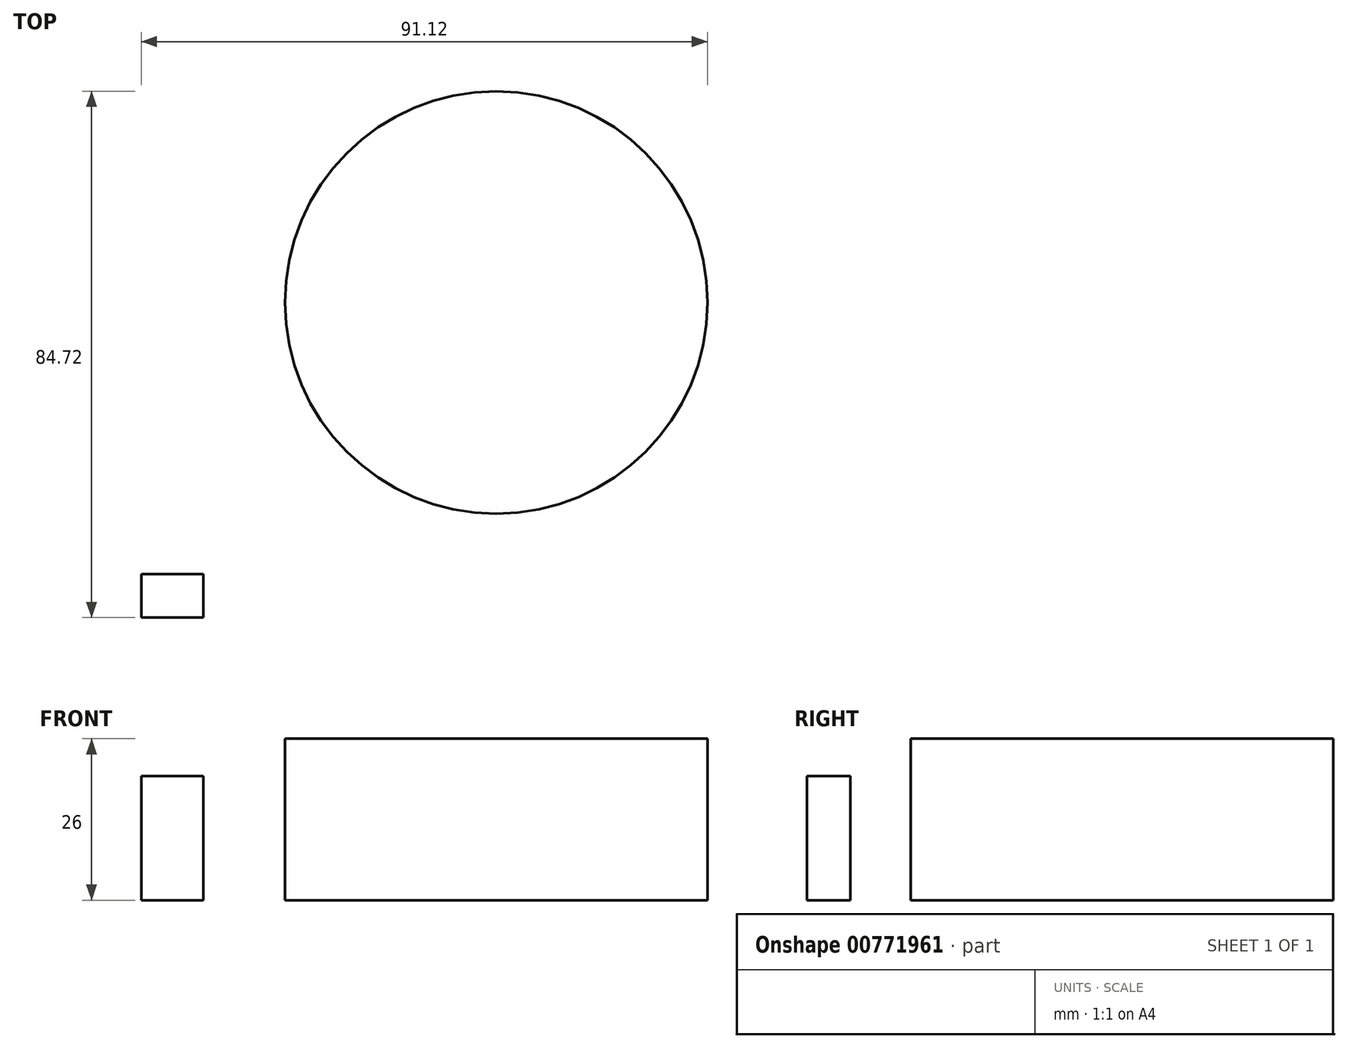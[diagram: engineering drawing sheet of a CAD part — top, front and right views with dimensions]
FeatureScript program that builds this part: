
annotation { "Feature Type Name" : "Feature", "Feature Type Description" : "" }
export const myFeature = defineFeature(function(context is Context, id is Id, definition is map)
    precondition{}
    {
        {
            var Q0;
            Q0=qCreatedBy(makeId("Top.planeOp"),FACE);
            var sketch = newSketch(context, id + "F0", { "sketchPlane" : qUnion([Q0])});
            skCircle(sketch, "E0", {"center": v(0, 0) * mm, "radius": 34 * mm});
            skCircle(sketch, "E1", {"center": v(0, 0) * mm, "radius": 1.5 * mm});
            skLineSegment(sketch, "E2", {"start": v(0, 1.5) * mm, "end": v(0, -1.5) * mm});
            skLineSegment(sketch, "E3", {"start": v(0, 1.5) * mm, "end": v(0, -1) * mm});
            skLineSegment(sketch, "E4", {"start": v(-1.12, -1) * mm, "end": v(1.12, -1) * mm});
            skSolve(sketch);
        }
        {
            var Q0;
            Q0 = qSketchRegion(id + "F0", true);
            var Q1;
            {var subQ0=sQuery(id+"F0.wireOp",EDGE,"E2");Q1=makeQuery(id+"F0.imprint","IMPRINT",FACE,{"disambiguationData":[TD([[makeQuery(id+"F0.imprint","IMPRINT",EDGE,{"derivedFrom":subQ0}),-1.0]])]});}
            var Q2;
            {var subQ0=sQuery(id+"F0.wireOp",EDGE,"E2");Q2=makeQuery(id+"F0.imprint","IMPRINT",FACE,{"disambiguationData":[TD([[makeQuery(id+"F0.imprint","IMPRINT",EDGE,{"derivedFrom":subQ0}),1.0]])]});}
            extrude(context, id + "F1", {"entities" : qUnion([Q0, Q1, Q2]), "depth" : 26 * mm, "offsetDistance" : 25 * mm});
        }
        {
            var Q0;
            Q0=qCreatedBy(makeId("Top.planeOp"),FACE);
            var sketch = newSketch(context, id + "F2", { "sketchPlane" : qUnion([Q0])});
            skCircle(sketch, "E5", {"center": v(-52.12, -47.22) * mm, "radius": 6.1 * mm});
            skLineSegment(sketch, "E6", {"start": v(-57.12, -43.72) * mm, "end": v(-57.12, -50.72) * mm});
            skLineSegment(sketch, "E7", {"start": v(-57.12, -50.72) * mm, "end": v(-47.12, -50.72) * mm});
            skLineSegment(sketch, "E8", {"start": v(-47.12, -50.72) * mm, "end": v(-47.12, -43.72) * mm});
            skLineSegment(sketch, "E9", {"start": v(-47.12, -43.72) * mm, "end": v(-57.12, -43.72) * mm});
            skSolve(sketch);
        }
        {
            var Q0;
            Q0=makeQuery(id+"F2.imprint","IMPRINT",FACE,{"disambiguationData":[TD([[makeQuery(id+"F2.imprint","IMPRINT",EDGE,{"derivedFrom":sQuery(id+"F2.wireOp",EDGE,"E6")}),1.0]])]});
            extrude(context, id + "F3", {"entities" : qUnion([Q0]), "depth" : 20 * mm, "offsetDistance" : 25 * mm});
        }
    });
